# Revit family: Windows_Blinds_Nimex_Solovent_CL1100
name_source: partatom
category: Specialty Equipment
revit_build: Autodesk Revit 2018 (Build: 20170223_1515(x64)
units: mm (PartAtom-declared; Revit-internal decimal feet)

## family parameters
Cut with Voids When Loaded = No
Host = Face
OmniClass Number = 23.40.10.14
OmniClass Title = Exterior Specialties
Part Type = Normal
Room Calculation Point = No
Round Connector Dimension = Use Diameter
Shared = No

## types (11) — shared parameters
AssetType = Fixed
BIMObjectName = Windows_Blinds_Nimex_Solovent_CL1100
Brand = Nimex
Category = Shutters
Color = Various
DurationUnit = Years
IfcExportAs = IfcShadingDeviceType
IfcExportType = BLIND
Manufacturer = Nimex
ManufacturerName = Nimex
ManufacturerURL = https://www.nimex.se
Material = Aluminum & plastic
NBSDescription = Shutter hardware system
NBSReference = 25-90-20/175
Name = Nimex_Solovent_CL1100
NominalHeight = 732 mm
NominalLength = 900 mm  [stored 2.95276 ft]
Shape = Sculptured
URL = https://www.nimex.se
Uniclass2 = Ss_25_50
Uniclass2015Description = Shutter systems
Uniclass2015Reference = Ss_25_50_80
Version = 1
VersionDate = 28/06/2021
WarrantyDurationUnit = Years
zero-valued in all types: Default Elevation

## per-type parameters (varying)
| type | NominalDepth | ObjectType | Size |
| CL1100 - 1800 mm | 1800 mm  [stored 5.90551 ft] | CL1100_1000+ | 500 - 4000 x 1800 x 735 mm |
| CL1100 - 1700 mm | 1700 mm  [stored 5.57743 ft] | CL1100_1000+ | 500 - 4000 x 1700 x 735 mm |
| CL1100 - 1600 mm | 1600 mm  [stored 5.24934 ft] | CL1100_1000+ | 500 - 4000 x 1600 x 735 mm |
| CL1100 - 1500 mm | 1500 mm  [stored 4.92126 ft] | CL1100_1000+ | 500 - 4000 x 1500 x 735 mm |
| CL1100 - 1400 mm | 1400 mm  [stored 4.59318 ft] | CL1100_1000+ | 500 - 4000 x 1400 x 735 mm |
| CL1100 - 1300 mm | 1300 mm  [stored 4.26509 ft] | CL1100_1000+ | 500 - 4000 x 1300 x 735 mm |
| CL1100 - 1200 mm | 1200 mm | CL1100_1000+ | 500 - 4000 x 1200 x 735 mm |
| CL1100 - 1100 mm | 1100 mm | CL1100_1000+ | 500 - 4000 x 1100 x 735 mm |
| CL1100 - 1000 mm | 1000 mm  [stored 3.28084 ft] | CL1100_1000+ | 500 - 4000 x 1000 x 735 mm |
| CL1100 - 900 mm | 900 mm  [stored 2.95276 ft] | CL1100_900 | 500 - 4000 x 900 x 735 mm |
| CL1100 - 800 mm | 800 mm  [stored 2.62467 ft] | CL1100_800 | 500 - 4000 x 800 x 735 mm |

note: column(s) folded — value = type name in every type: Model

note: [stored X ft] marks values corroborated as IEEE doubles in the binary element streams (Revit-internal decimal feet)

## geometry (parser evidence)
native form markers: Sweep x12
no freeform markers — native parametric forms only
